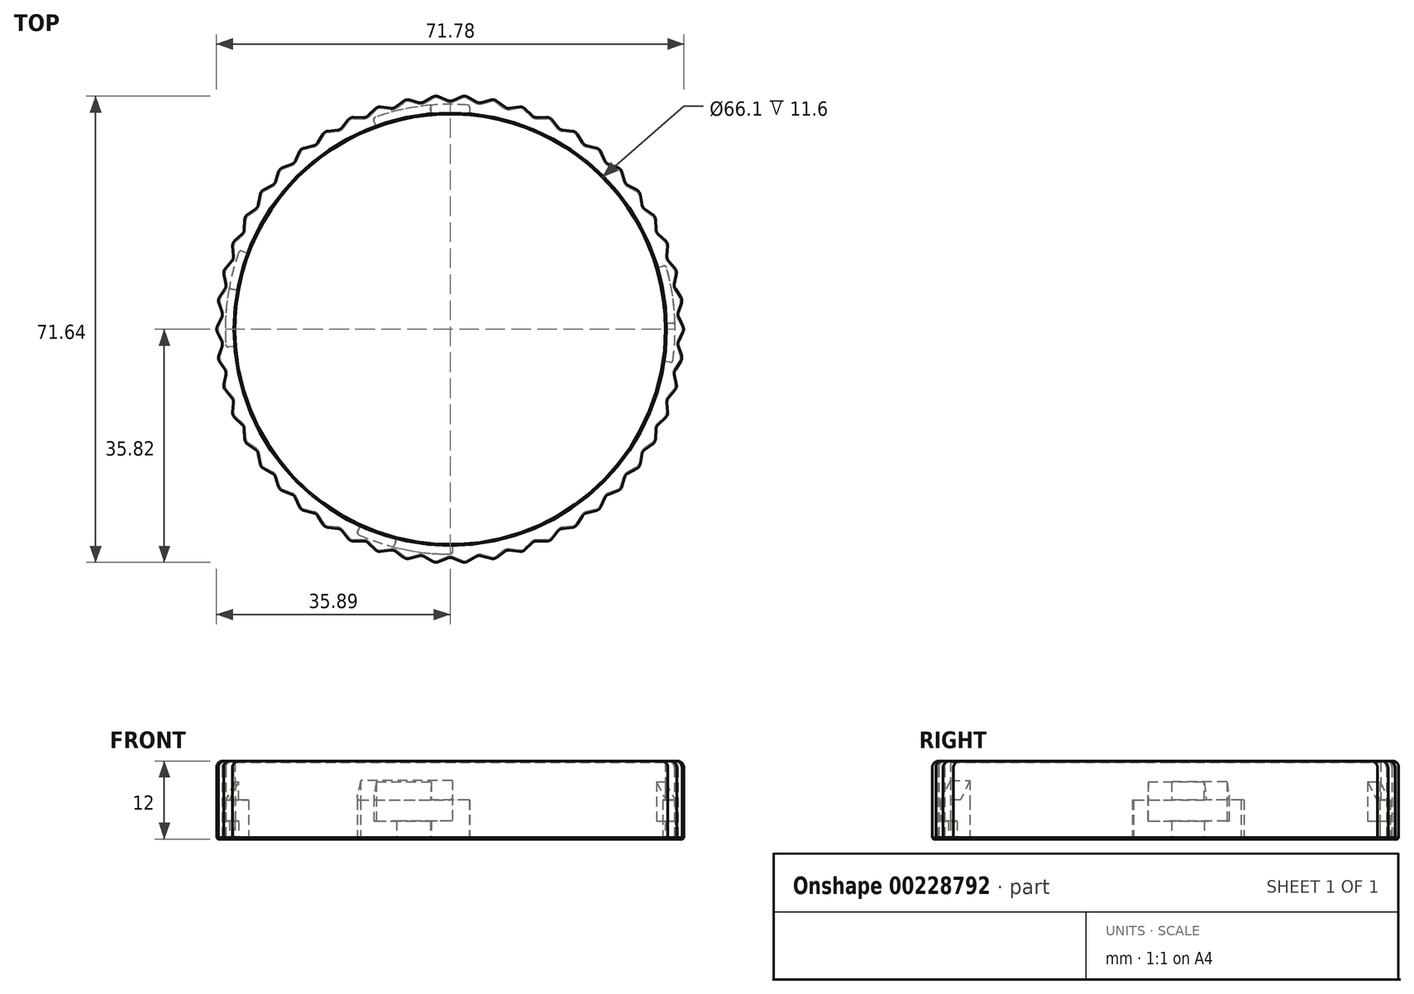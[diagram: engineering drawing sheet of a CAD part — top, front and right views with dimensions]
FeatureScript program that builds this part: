
annotation { "Feature Type Name" : "Feature", "Feature Type Description" : "" }
export const myFeature = defineFeature(function(context is Context, id is Id, definition is map)
    precondition{}
    {
        {
            var Q0;
            Q0=qCreatedBy(makeId("Top.planeOp"),FACE);
            var sketch = newSketch(context, id + "F0", { "sketchPlane" : qUnion([Q0])});
            skCircle(sketch, "E0", {"center": v(0, 0) * mm, "radius": 33.05 * mm});
            skLineSegment(sketch, "E1", {"start": v(2.68, 35.69) * mm, "end": v(4.03, 34.93) * mm});
            skLineSegment(sketch, "E2", {"start": v(4.78, 34.83) * mm, "end": v(6.28, 35.24) * mm});
            skPoint(sketch, "E3.visualSharp", {"position": v(2.26, 35.93) * mm});
            skArc(sketch, "E3.filletArc", {"start": v(2.68, 35.69) * mm, "mid": v(2.25, 35.82) * mm, "end": v(1.81, 35.74) * mm});
            skPoint(sketch, "E4.visualSharp", {"position": v(4.39, 34.72) * mm});
            skArc(sketch, "E4.filletArc", {"start": v(4.03, 34.93) * mm, "mid": v(4.4, 34.8) * mm, "end": v(4.78, 34.83) * mm});
            skPoint(sketch, "E5.visualSharp", {"position": v(6.75, 35.36) * mm});
            skArc(sketch, "E5.filletArc", {"start": v(6.72, 35.25) * mm, "mid": v(6.5, 35.27) * mm, "end": v(6.28, 35.24) * mm});
            skLineSegment(sketch, "E6.1.0", {"start": v(-1.81, 35.74) * mm, "end": v(-0.38, 35.16) * mm});
            skPoint(sketch, "E6.1.1", {"position": v(0, 35) * mm});
            skPoint(sketch, "E6.1.2", {"position": v(-2.26, 35.93) * mm});
            skArc(sketch, "E6.1.4", {"start": v(-0.38, 35.16) * mm, "mid": v(0, 35.08) * mm, "end": v(0.38, 35.16) * mm});
            skLineSegment(sketch, "E6.1.5", {"start": v(0.38, 35.16) * mm, "end": v(1.81, 35.74) * mm});
            skArc(sketch, "E6.1.6", {"start": v(-1.81, 35.74) * mm, "mid": v(-2.25, 35.82) * mm, "end": v(-2.68, 35.69) * mm});
            skArc(sketch, "E6.1.7", {"start": v(2.25, 35.82) * mm, "mid": v(2.03, 35.8) * mm, "end": v(1.81, 35.74) * mm});
            skLineSegment(sketch, "E6.2.0", {"start": v(-6.28, 35.24) * mm, "end": v(-4.78, 34.83) * mm});
            skPoint(sketch, "E6.2.1", {"position": v(-4.39, 34.72) * mm});
            skPoint(sketch, "E6.2.2", {"position": v(-6.75, 35.36) * mm});
            skPoint(sketch, "E6.2.3", {"position": v(-2.26, 35.93) * mm});
            skArc(sketch, "E6.2.4", {"start": v(-4.78, 34.83) * mm, "mid": v(-4.4, 34.8) * mm, "end": v(-4.03, 34.93) * mm});
            skLineSegment(sketch, "E6.2.5", {"start": v(-4.03, 34.93) * mm, "end": v(-2.68, 35.69) * mm});
            skArc(sketch, "E6.2.6", {"start": v(-6.28, 35.24) * mm, "mid": v(-6.72, 35.25) * mm, "end": v(-7.14, 35.07) * mm});
            skArc(sketch, "E6.2.7", {"start": v(-2.25, 35.82) * mm, "mid": v(-2.48, 35.78) * mm, "end": v(-2.68, 35.69) * mm});
            skLineSegment(sketch, "E6.3.0", {"start": v(-10.64, 34.17) * mm, "end": v(-9.11, 33.96) * mm});
            skPoint(sketch, "E6.3.1", {"position": v(-8.7, 33.9) * mm});
            skPoint(sketch, "E6.3.2", {"position": v(-11.12, 34.24) * mm});
            skPoint(sketch, "E6.3.3", {"position": v(-6.75, 35.36) * mm});
            skArc(sketch, "E6.3.4", {"start": v(-9.11, 33.96) * mm, "mid": v(-8.72, 33.98) * mm, "end": v(-8.37, 34.15) * mm});
            skLineSegment(sketch, "E6.3.5", {"start": v(-8.37, 34.15) * mm, "end": v(-7.14, 35.07) * mm});
            skArc(sketch, "E6.3.6", {"start": v(-10.64, 34.17) * mm, "mid": v(-11.09, 34.13) * mm, "end": v(-11.47, 33.9) * mm});
            skArc(sketch, "E6.3.7", {"start": v(-6.72, 35.25) * mm, "mid": v(-6.94, 35.19) * mm, "end": v(-7.14, 35.07) * mm});
            skLineSegment(sketch, "E6.4.0", {"start": v(-14.84, 32.57) * mm, "end": v(-13.3, 32.55) * mm});
            skPoint(sketch, "E6.4.1", {"position": v(-12.88, 32.54) * mm});
            skPoint(sketch, "E6.4.2", {"position": v(-15.33, 32.57) * mm});
            skPoint(sketch, "E6.4.3", {"position": v(-11.12, 34.24) * mm});
            skArc(sketch, "E6.4.4", {"start": v(-13.3, 32.55) * mm, "mid": v(-12.91, 32.62) * mm, "end": v(-12.59, 32.83) * mm});
            skLineSegment(sketch, "E6.4.5", {"start": v(-12.59, 32.83) * mm, "end": v(-11.47, 33.9) * mm});
            skArc(sketch, "E6.4.6", {"start": v(-14.84, 32.57) * mm, "mid": v(-15.28, 32.47) * mm, "end": v(-15.63, 32.2) * mm});
            skArc(sketch, "E6.4.7", {"start": v(-11.09, 34.13) * mm, "mid": v(-11.3, 34.04) * mm, "end": v(-11.47, 33.9) * mm});
            skLineSegment(sketch, "E6.5.0", {"start": v(-18.8, 30.45) * mm, "end": v(-17.27, 30.62) * mm});
            skPoint(sketch, "E6.5.1", {"position": v(-16.86, 30.67) * mm});
            skPoint(sketch, "E6.5.2", {"position": v(-19.29, 30.4) * mm});
            skPoint(sketch, "E6.5.3", {"position": v(-15.33, 32.57) * mm});
            skArc(sketch, "E6.5.4", {"start": v(-17.27, 30.62) * mm, "mid": v(-16.9, 30.74) * mm, "end": v(-16.6, 31) * mm});
            skLineSegment(sketch, "E6.5.5", {"start": v(-16.6, 31) * mm, "end": v(-15.63, 32.2) * mm});
            skArc(sketch, "E6.5.6", {"start": v(-18.8, 30.45) * mm, "mid": v(-19.23, 30.3) * mm, "end": v(-19.55, 29.98) * mm});
            skArc(sketch, "E6.5.7", {"start": v(-15.28, 32.47) * mm, "mid": v(-15.47, 32.35) * mm, "end": v(-15.63, 32.2) * mm});
            skLineSegment(sketch, "E6.6.0", {"start": v(-22.47, 27.85) * mm, "end": v(-20.97, 28.22) * mm});
            skPoint(sketch, "E6.6.1", {"position": v(-20.57, 28.32) * mm});
            skPoint(sketch, "E6.6.2", {"position": v(-22.95, 27.74) * mm});
            skPoint(sketch, "E6.6.3", {"position": v(-19.29, 30.4) * mm});
            skArc(sketch, "E6.6.4", {"start": v(-20.97, 28.22) * mm, "mid": v(-20.62, 28.38) * mm, "end": v(-20.36, 28.67) * mm});
            skLineSegment(sketch, "E6.6.5", {"start": v(-20.36, 28.67) * mm, "end": v(-19.55, 29.98) * mm});
            skArc(sketch, "E6.6.6", {"start": v(-22.47, 27.85) * mm, "mid": v(-22.88, 27.65) * mm, "end": v(-23.15, 27.3) * mm});
            skArc(sketch, "E6.6.7", {"start": v(-19.23, 30.3) * mm, "mid": v(-19.4, 30.16) * mm, "end": v(-19.55, 29.98) * mm});
            skLineSegment(sketch, "E6.7.0", {"start": v(-25.79, 24.82) * mm, "end": v(-24.34, 25.37) * mm});
            skPoint(sketch, "E6.7.1", {"position": v(-23.96, 25.51) * mm});
            skPoint(sketch, "E6.7.2", {"position": v(-26.24, 24.64) * mm});
            skPoint(sketch, "E6.7.3", {"position": v(-22.95, 27.74) * mm});
            skArc(sketch, "E6.7.4", {"start": v(-24.34, 25.37) * mm, "mid": v(-24.01, 25.57) * mm, "end": v(-23.79, 25.89) * mm});
            skLineSegment(sketch, "E6.7.5", {"start": v(-23.79, 25.89) * mm, "end": v(-23.15, 27.3) * mm});
            skArc(sketch, "E6.7.6", {"start": v(-25.79, 24.82) * mm, "mid": v(-26.16, 24.57) * mm, "end": v(-26.39, 24.18) * mm});
            skArc(sketch, "E6.7.7", {"start": v(-22.88, 27.65) * mm, "mid": v(-23.03, 27.49) * mm, "end": v(-23.15, 27.3) * mm});
            skLineSegment(sketch, "E6.8.0", {"start": v(-28.7, 21.39) * mm, "end": v(-27.33, 22.12) * mm});
            skPoint(sketch, "E6.8.1", {"position": v(-26.97, 22.3) * mm});
            skPoint(sketch, "E6.8.2", {"position": v(-29.12, 21.16) * mm});
            skPoint(sketch, "E6.8.3", {"position": v(-26.24, 24.64) * mm});
            skArc(sketch, "E6.8.4", {"start": v(-27.33, 22.12) * mm, "mid": v(-27.03, 22.36) * mm, "end": v(-26.85, 22.7) * mm});
            skLineSegment(sketch, "E6.8.5", {"start": v(-26.85, 22.7) * mm, "end": v(-26.39, 24.18) * mm});
            skArc(sketch, "E6.8.6", {"start": v(-28.7, 21.39) * mm, "mid": v(-29.03, 21.1) * mm, "end": v(-29.2, 20.68) * mm});
            skArc(sketch, "E6.8.7", {"start": v(-26.16, 24.57) * mm, "mid": v(-26.3, 24.39) * mm, "end": v(-26.39, 24.18) * mm});
            skLineSegment(sketch, "E6.9.0", {"start": v(-31.15, 17.62) * mm, "end": v(-29.89, 18.52) * mm});
            skPoint(sketch, "E6.9.1", {"position": v(-29.55, 18.75) * mm});
            skPoint(sketch, "E6.9.2", {"position": v(-31.55, 17.34) * mm});
            skPoint(sketch, "E6.9.3", {"position": v(-29.12, 21.16) * mm});
            skArc(sketch, "E6.9.4", {"start": v(-29.89, 18.52) * mm, "mid": v(-29.62, 18.8) * mm, "end": v(-29.48, 19.16) * mm});
            skLineSegment(sketch, "E6.9.5", {"start": v(-29.48, 19.16) * mm, "end": v(-29.2, 20.68) * mm});
            skArc(sketch, "E6.9.6", {"start": v(-31.15, 17.62) * mm, "mid": v(-31.45, 17.29) * mm, "end": v(-31.57, 16.86) * mm});
            skArc(sketch, "E6.9.7", {"start": v(-29.03, 21.1) * mm, "mid": v(-29.15, 20.9) * mm, "end": v(-29.2, 20.68) * mm});
            skLineSegment(sketch, "E6.10.0", {"start": v(-33.11, 13.58) * mm, "end": v(-31.97, 14.62) * mm});
            skPoint(sketch, "E6.10.1", {"position": v(-31.67, 14.9) * mm});
            skPoint(sketch, "E6.10.2", {"position": v(-33.47, 13.25) * mm});
            skPoint(sketch, "E6.10.3", {"position": v(-31.55, 17.34) * mm});
            skArc(sketch, "E6.10.4", {"start": v(-31.97, 14.62) * mm, "mid": v(-31.74, 14.94) * mm, "end": v(-31.65, 15.31) * mm});
            skLineSegment(sketch, "E6.10.5", {"start": v(-31.65, 15.31) * mm, "end": v(-31.57, 16.86) * mm});
            skArc(sketch, "E6.10.6", {"start": v(-33.11, 13.58) * mm, "mid": v(-33.37, 13.21) * mm, "end": v(-33.44, 12.77) * mm});
            skArc(sketch, "E6.10.7", {"start": v(-31.45, 17.29) * mm, "mid": v(-31.53, 17.08) * mm, "end": v(-31.57, 16.86) * mm});
            skLineSegment(sketch, "E6.11.0", {"start": v(-34.55, 9.32) * mm, "end": v(-33.55, 10.5) * mm});
            skPoint(sketch, "E6.11.1", {"position": v(-33.29, 10.82) * mm});
            skPoint(sketch, "E6.11.2", {"position": v(-34.87, 8.95) * mm});
            skPoint(sketch, "E6.11.3", {"position": v(-33.47, 13.25) * mm});
            skArc(sketch, "E6.11.4", {"start": v(-33.55, 10.5) * mm, "mid": v(-33.36, 10.84) * mm, "end": v(-33.32, 11.23) * mm});
            skLineSegment(sketch, "E6.11.5", {"start": v(-33.32, 11.23) * mm, "end": v(-33.44, 12.77) * mm});
            skArc(sketch, "E6.11.6", {"start": v(-34.55, 9.32) * mm, "mid": v(-34.76, 8.92) * mm, "end": v(-34.77, 8.48) * mm});
            skArc(sketch, "E6.11.7", {"start": v(-33.37, 13.21) * mm, "mid": v(-33.43, 13) * mm, "end": v(-33.44, 12.77) * mm});
            skLineSegment(sketch, "E6.12.0", {"start": v(-35.45, 4.92) * mm, "end": v(-34.6, 6.21) * mm});
            skPoint(sketch, "E6.12.1", {"position": v(-34.38, 6.56) * mm});
            skPoint(sketch, "E6.12.2", {"position": v(-35.72, 4.51) * mm});
            skPoint(sketch, "E6.12.3", {"position": v(-34.87, 8.95) * mm});
            skArc(sketch, "E6.12.4", {"start": v(-34.6, 6.21) * mm, "mid": v(-34.46, 6.57) * mm, "end": v(-34.46, 6.96) * mm});
            skLineSegment(sketch, "E6.12.5", {"start": v(-34.46, 6.96) * mm, "end": v(-34.77, 8.48) * mm});
            skArc(sketch, "E6.12.6", {"start": v(-35.45, 4.92) * mm, "mid": v(-35.6, 4.5) * mm, "end": v(-35.56, 4.05) * mm});
            skArc(sketch, "E6.12.7", {"start": v(-34.76, 8.92) * mm, "mid": v(-34.8, 8.7) * mm, "end": v(-34.77, 8.48) * mm});
            skLineSegment(sketch, "E6.13.0", {"start": v(-35.79, 0.44) * mm, "end": v(-35.11, 1.83) * mm});
            skPoint(sketch, "E6.13.1", {"position": v(-34.93, 2.2) * mm});
            skPoint(sketch, "E6.13.2", {"position": v(-36, 0) * mm});
            skPoint(sketch, "E6.13.3", {"position": v(-35.72, 4.51) * mm});
            skArc(sketch, "E6.13.4", {"start": v(-35.11, 1.83) * mm, "mid": v(-35.01, 2.2) * mm, "end": v(-35.06, 2.59) * mm});
            skLineSegment(sketch, "E6.13.5", {"start": v(-35.06, 2.59) * mm, "end": v(-35.56, 4.05) * mm});
            skArc(sketch, "E6.13.6", {"start": v(-35.79, 0.44) * mm, "mid": v(-35.89, 0) * mm, "end": v(-35.79, -0.44) * mm});
            skArc(sketch, "E6.13.7", {"start": v(-35.6, 4.5) * mm, "mid": v(-35.6, 4.27) * mm, "end": v(-35.56, 4.05) * mm});
            skLineSegment(sketch, "E6.14.0", {"start": v(-35.56, -4.05) * mm, "end": v(-35.06, -2.59) * mm});
            skPoint(sketch, "E6.14.1", {"position": v(-34.93, -2.2) * mm});
            skPoint(sketch, "E6.14.2", {"position": v(-35.72, -4.51) * mm});
            skPoint(sketch, "E6.14.3", {"position": v(-36, 0) * mm});
            skArc(sketch, "E6.14.4", {"start": v(-35.06, -2.59) * mm, "mid": v(-35.01, -2.2) * mm, "end": v(-35.11, -1.83) * mm});
            skLineSegment(sketch, "E6.14.5", {"start": v(-35.11, -1.83) * mm, "end": v(-35.79, -0.44) * mm});
            skArc(sketch, "E6.14.6", {"start": v(-35.56, -4.05) * mm, "mid": v(-35.6, -4.5) * mm, "end": v(-35.45, -4.92) * mm});
            skArc(sketch, "E6.14.7", {"start": v(-35.89, 0) * mm, "mid": v(-35.86, -0.22) * mm, "end": v(-35.79, -0.44) * mm});
            skLineSegment(sketch, "E6.15.0", {"start": v(-34.77, -8.48) * mm, "end": v(-34.46, -6.96) * mm});
            skPoint(sketch, "E6.15.1", {"position": v(-34.38, -6.56) * mm});
            skPoint(sketch, "E6.15.2", {"position": v(-34.87, -8.95) * mm});
            skPoint(sketch, "E6.15.3", {"position": v(-35.72, -4.51) * mm});
            skArc(sketch, "E6.15.4", {"start": v(-34.46, -6.96) * mm, "mid": v(-34.46, -6.57) * mm, "end": v(-34.6, -6.21) * mm});
            skLineSegment(sketch, "E6.15.5", {"start": v(-34.6, -6.21) * mm, "end": v(-35.45, -4.92) * mm});
            skArc(sketch, "E6.15.6", {"start": v(-34.77, -8.48) * mm, "mid": v(-34.76, -8.92) * mm, "end": v(-34.55, -9.32) * mm});
            skArc(sketch, "E6.15.7", {"start": v(-35.6, -4.5) * mm, "mid": v(-35.55, -4.72) * mm, "end": v(-35.45, -4.92) * mm});
            skLineSegment(sketch, "E6.16.0", {"start": v(-33.44, -12.77) * mm, "end": v(-33.32, -11.23) * mm});
            skPoint(sketch, "E6.16.1", {"position": v(-33.29, -10.82) * mm});
            skPoint(sketch, "E6.16.2", {"position": v(-33.47, -13.25) * mm});
            skPoint(sketch, "E6.16.3", {"position": v(-34.87, -8.95) * mm});
            skArc(sketch, "E6.16.4", {"start": v(-33.32, -11.23) * mm, "mid": v(-33.36, -10.84) * mm, "end": v(-33.55, -10.5) * mm});
            skLineSegment(sketch, "E6.16.5", {"start": v(-33.55, -10.5) * mm, "end": v(-34.55, -9.32) * mm});
            skArc(sketch, "E6.16.6", {"start": v(-33.44, -12.77) * mm, "mid": v(-33.37, -13.21) * mm, "end": v(-33.11, -13.58) * mm});
            skArc(sketch, "E6.16.7", {"start": v(-34.76, -8.92) * mm, "mid": v(-34.68, -9.14) * mm, "end": v(-34.55, -9.32) * mm});
            skLineSegment(sketch, "E6.17.0", {"start": v(-31.57, -16.86) * mm, "end": v(-31.65, -15.31) * mm});
            skPoint(sketch, "E6.17.1", {"position": v(-31.67, -14.9) * mm});
            skPoint(sketch, "E6.17.2", {"position": v(-31.55, -17.34) * mm});
            skPoint(sketch, "E6.17.3", {"position": v(-33.47, -13.25) * mm});
            skArc(sketch, "E6.17.4", {"start": v(-31.65, -15.31) * mm, "mid": v(-31.74, -14.94) * mm, "end": v(-31.97, -14.62) * mm});
            skLineSegment(sketch, "E6.17.5", {"start": v(-31.97, -14.62) * mm, "end": v(-33.11, -13.58) * mm});
            skArc(sketch, "E6.17.6", {"start": v(-31.57, -16.86) * mm, "mid": v(-31.45, -17.29) * mm, "end": v(-31.15, -17.62) * mm});
            skArc(sketch, "E6.17.7", {"start": v(-33.37, -13.21) * mm, "mid": v(-33.26, -13.41) * mm, "end": v(-33.11, -13.58) * mm});
            skLineSegment(sketch, "E6.18.0", {"start": v(-29.2, -20.68) * mm, "end": v(-29.48, -19.16) * mm});
            skPoint(sketch, "E6.18.1", {"position": v(-29.55, -18.75) * mm});
            skPoint(sketch, "E6.18.2", {"position": v(-29.12, -21.16) * mm});
            skPoint(sketch, "E6.18.3", {"position": v(-31.55, -17.34) * mm});
            skArc(sketch, "E6.18.4", {"start": v(-29.48, -19.16) * mm, "mid": v(-29.62, -18.8) * mm, "end": v(-29.89, -18.52) * mm});
            skLineSegment(sketch, "E6.18.5", {"start": v(-29.89, -18.52) * mm, "end": v(-31.15, -17.62) * mm});
            skArc(sketch, "E6.18.6", {"start": v(-29.2, -20.68) * mm, "mid": v(-29.03, -21.1) * mm, "end": v(-28.7, -21.39) * mm});
            skArc(sketch, "E6.18.7", {"start": v(-31.45, -17.29) * mm, "mid": v(-31.32, -17.47) * mm, "end": v(-31.15, -17.62) * mm});
            skLineSegment(sketch, "E6.19.0", {"start": v(-26.39, -24.18) * mm, "end": v(-26.85, -22.7) * mm});
            skPoint(sketch, "E6.19.1", {"position": v(-26.97, -22.3) * mm});
            skPoint(sketch, "E6.19.2", {"position": v(-26.24, -24.64) * mm});
            skPoint(sketch, "E6.19.3", {"position": v(-29.12, -21.16) * mm});
            skArc(sketch, "E6.19.4", {"start": v(-26.85, -22.7) * mm, "mid": v(-27.03, -22.36) * mm, "end": v(-27.33, -22.12) * mm});
            skLineSegment(sketch, "E6.19.5", {"start": v(-27.33, -22.12) * mm, "end": v(-28.7, -21.39) * mm});
            skArc(sketch, "E6.19.6", {"start": v(-26.39, -24.18) * mm, "mid": v(-26.16, -24.57) * mm, "end": v(-25.79, -24.82) * mm});
            skArc(sketch, "E6.19.7", {"start": v(-29.03, -21.1) * mm, "mid": v(-28.88, -21.26) * mm, "end": v(-28.7, -21.39) * mm});
            skLineSegment(sketch, "E6.20.0", {"start": v(-23.15, -27.3) * mm, "end": v(-23.79, -25.89) * mm});
            skPoint(sketch, "E6.20.1", {"position": v(-23.96, -25.51) * mm});
            skPoint(sketch, "E6.20.2", {"position": v(-22.95, -27.74) * mm});
            skPoint(sketch, "E6.20.3", {"position": v(-26.24, -24.64) * mm});
            skArc(sketch, "E6.20.4", {"start": v(-23.79, -25.89) * mm, "mid": v(-24.01, -25.57) * mm, "end": v(-24.34, -25.37) * mm});
            skLineSegment(sketch, "E6.20.5", {"start": v(-24.34, -25.37) * mm, "end": v(-25.79, -24.82) * mm});
            skArc(sketch, "E6.20.6", {"start": v(-23.15, -27.3) * mm, "mid": v(-22.88, -27.65) * mm, "end": v(-22.47, -27.85) * mm});
            skArc(sketch, "E6.20.7", {"start": v(-26.16, -24.57) * mm, "mid": v(-25.99, -24.71) * mm, "end": v(-25.79, -24.82) * mm});
            skLineSegment(sketch, "E6.21.0", {"start": v(-19.55, -29.98) * mm, "end": v(-20.36, -28.67) * mm});
            skPoint(sketch, "E6.21.1", {"position": v(-20.57, -28.32) * mm});
            skPoint(sketch, "E6.21.2", {"position": v(-19.29, -30.4) * mm});
            skPoint(sketch, "E6.21.3", {"position": v(-22.95, -27.74) * mm});
            skArc(sketch, "E6.21.4", {"start": v(-20.36, -28.67) * mm, "mid": v(-20.62, -28.38) * mm, "end": v(-20.97, -28.22) * mm});
            skLineSegment(sketch, "E6.21.5", {"start": v(-20.97, -28.22) * mm, "end": v(-22.47, -27.85) * mm});
            skArc(sketch, "E6.21.6", {"start": v(-19.55, -29.98) * mm, "mid": v(-19.23, -30.3) * mm, "end": v(-18.8, -30.45) * mm});
            skArc(sketch, "E6.21.7", {"start": v(-22.88, -27.65) * mm, "mid": v(-22.69, -27.78) * mm, "end": v(-22.47, -27.85) * mm});
            skLineSegment(sketch, "E6.22.0", {"start": v(-15.63, -32.2) * mm, "end": v(-16.6, -31) * mm});
            skPoint(sketch, "E6.22.1", {"position": v(-16.86, -30.67) * mm});
            skPoint(sketch, "E6.22.2", {"position": v(-15.33, -32.57) * mm});
            skPoint(sketch, "E6.22.3", {"position": v(-19.29, -30.4) * mm});
            skArc(sketch, "E6.22.4", {"start": v(-16.6, -31) * mm, "mid": v(-16.9, -30.74) * mm, "end": v(-17.27, -30.62) * mm});
            skLineSegment(sketch, "E6.22.5", {"start": v(-17.27, -30.62) * mm, "end": v(-18.8, -30.45) * mm});
            skArc(sketch, "E6.22.6", {"start": v(-15.63, -32.2) * mm, "mid": v(-15.28, -32.47) * mm, "end": v(-14.84, -32.57) * mm});
            skArc(sketch, "E6.22.7", {"start": v(-19.23, -30.3) * mm, "mid": v(-19.03, -30.4) * mm, "end": v(-18.8, -30.45) * mm});
            skLineSegment(sketch, "E6.23.0", {"start": v(-11.47, -33.9) * mm, "end": v(-12.59, -32.83) * mm});
            skPoint(sketch, "E6.23.1", {"position": v(-12.88, -32.54) * mm});
            skPoint(sketch, "E6.23.2", {"position": v(-11.12, -34.24) * mm});
            skPoint(sketch, "E6.23.3", {"position": v(-15.33, -32.57) * mm});
            skArc(sketch, "E6.23.4", {"start": v(-12.59, -32.83) * mm, "mid": v(-12.91, -32.62) * mm, "end": v(-13.3, -32.55) * mm});
            skLineSegment(sketch, "E6.23.5", {"start": v(-13.3, -32.55) * mm, "end": v(-14.84, -32.57) * mm});
            skArc(sketch, "E6.23.6", {"start": v(-11.47, -33.9) * mm, "mid": v(-11.09, -34.13) * mm, "end": v(-10.64, -34.17) * mm});
            skArc(sketch, "E6.23.7", {"start": v(-15.28, -32.47) * mm, "mid": v(-15.07, -32.54) * mm, "end": v(-14.84, -32.57) * mm});
            skLineSegment(sketch, "E6.24.0", {"start": v(-7.14, -35.07) * mm, "end": v(-8.37, -34.15) * mm});
            skPoint(sketch, "E6.24.1", {"position": v(-8.7, -33.9) * mm});
            skPoint(sketch, "E6.24.2", {"position": v(-6.75, -35.36) * mm});
            skPoint(sketch, "E6.24.3", {"position": v(-11.12, -34.24) * mm});
            skArc(sketch, "E6.24.4", {"start": v(-8.37, -34.15) * mm, "mid": v(-8.72, -33.98) * mm, "end": v(-9.11, -33.96) * mm});
            skLineSegment(sketch, "E6.24.5", {"start": v(-9.11, -33.96) * mm, "end": v(-10.64, -34.17) * mm});
            skArc(sketch, "E6.24.6", {"start": v(-7.14, -35.07) * mm, "mid": v(-6.72, -35.25) * mm, "end": v(-6.28, -35.24) * mm});
            skArc(sketch, "E6.24.7", {"start": v(-11.09, -34.13) * mm, "mid": v(-10.87, -34.18) * mm, "end": v(-10.64, -34.17) * mm});
            skLineSegment(sketch, "E6.25.0", {"start": v(-2.68, -35.69) * mm, "end": v(-4.03, -34.93) * mm});
            skPoint(sketch, "E6.25.1", {"position": v(-4.39, -34.72) * mm});
            skPoint(sketch, "E6.25.2", {"position": v(-2.26, -35.93) * mm});
            skPoint(sketch, "E6.25.3", {"position": v(-6.75, -35.36) * mm});
            skArc(sketch, "E6.25.4", {"start": v(-4.03, -34.93) * mm, "mid": v(-4.4, -34.8) * mm, "end": v(-4.78, -34.83) * mm});
            skLineSegment(sketch, "E6.25.5", {"start": v(-4.78, -34.83) * mm, "end": v(-6.28, -35.24) * mm});
            skArc(sketch, "E6.25.6", {"start": v(-2.68, -35.69) * mm, "mid": v(-2.25, -35.82) * mm, "end": v(-1.81, -35.74) * mm});
            skArc(sketch, "E6.25.7", {"start": v(-6.72, -35.25) * mm, "mid": v(-6.5, -35.27) * mm, "end": v(-6.28, -35.24) * mm});
            skLineSegment(sketch, "E6.26.0", {"start": v(1.81, -35.74) * mm, "end": v(0.38, -35.16) * mm});
            skPoint(sketch, "E6.26.1", {"position": v(0, -35) * mm});
            skPoint(sketch, "E6.26.2", {"position": v(2.26, -35.93) * mm});
            skPoint(sketch, "E6.26.3", {"position": v(-2.26, -35.93) * mm});
            skArc(sketch, "E6.26.4", {"start": v(0.38, -35.16) * mm, "mid": v(0, -35.08) * mm, "end": v(-0.38, -35.16) * mm});
            skLineSegment(sketch, "E6.26.5", {"start": v(-0.38, -35.16) * mm, "end": v(-1.81, -35.74) * mm});
            skArc(sketch, "E6.26.6", {"start": v(1.81, -35.74) * mm, "mid": v(2.25, -35.82) * mm, "end": v(2.68, -35.69) * mm});
            skArc(sketch, "E6.26.7", {"start": v(-2.25, -35.82) * mm, "mid": v(-2.03, -35.8) * mm, "end": v(-1.81, -35.74) * mm});
            skLineSegment(sketch, "E6.27.0", {"start": v(6.28, -35.24) * mm, "end": v(4.78, -34.83) * mm});
            skPoint(sketch, "E6.27.1", {"position": v(4.39, -34.72) * mm});
            skPoint(sketch, "E6.27.2", {"position": v(6.75, -35.36) * mm});
            skPoint(sketch, "E6.27.3", {"position": v(2.26, -35.93) * mm});
            skArc(sketch, "E6.27.4", {"start": v(4.78, -34.83) * mm, "mid": v(4.4, -34.8) * mm, "end": v(4.03, -34.93) * mm});
            skLineSegment(sketch, "E6.27.5", {"start": v(4.03, -34.93) * mm, "end": v(2.68, -35.69) * mm});
            skArc(sketch, "E6.27.6", {"start": v(6.28, -35.24) * mm, "mid": v(6.72, -35.25) * mm, "end": v(7.14, -35.07) * mm});
            skArc(sketch, "E6.27.7", {"start": v(2.25, -35.82) * mm, "mid": v(2.48, -35.78) * mm, "end": v(2.68, -35.69) * mm});
            skLineSegment(sketch, "E6.28.0", {"start": v(10.64, -34.17) * mm, "end": v(9.11, -33.96) * mm});
            skPoint(sketch, "E6.28.1", {"position": v(8.7, -33.9) * mm});
            skPoint(sketch, "E6.28.2", {"position": v(11.12, -34.24) * mm});
            skPoint(sketch, "E6.28.3", {"position": v(6.75, -35.36) * mm});
            skArc(sketch, "E6.28.4", {"start": v(9.11, -33.96) * mm, "mid": v(8.72, -33.98) * mm, "end": v(8.37, -34.15) * mm});
            skLineSegment(sketch, "E6.28.5", {"start": v(8.37, -34.15) * mm, "end": v(7.14, -35.07) * mm});
            skArc(sketch, "E6.28.6", {"start": v(10.64, -34.17) * mm, "mid": v(11.09, -34.13) * mm, "end": v(11.47, -33.9) * mm});
            skArc(sketch, "E6.28.7", {"start": v(6.72, -35.25) * mm, "mid": v(6.94, -35.19) * mm, "end": v(7.14, -35.07) * mm});
            skLineSegment(sketch, "E6.29.0", {"start": v(14.84, -32.57) * mm, "end": v(13.3, -32.55) * mm});
            skPoint(sketch, "E6.29.1", {"position": v(12.88, -32.54) * mm});
            skPoint(sketch, "E6.29.2", {"position": v(15.33, -32.57) * mm});
            skPoint(sketch, "E6.29.3", {"position": v(11.12, -34.24) * mm});
            skArc(sketch, "E6.29.4", {"start": v(13.3, -32.55) * mm, "mid": v(12.91, -32.62) * mm, "end": v(12.59, -32.83) * mm});
            skLineSegment(sketch, "E6.29.5", {"start": v(12.59, -32.83) * mm, "end": v(11.47, -33.9) * mm});
            skArc(sketch, "E6.29.6", {"start": v(14.84, -32.57) * mm, "mid": v(15.28, -32.47) * mm, "end": v(15.63, -32.2) * mm});
            skArc(sketch, "E6.29.7", {"start": v(11.09, -34.13) * mm, "mid": v(11.3, -34.04) * mm, "end": v(11.47, -33.9) * mm});
            skLineSegment(sketch, "E6.30.0", {"start": v(18.8, -30.45) * mm, "end": v(17.27, -30.62) * mm});
            skPoint(sketch, "E6.30.1", {"position": v(16.86, -30.67) * mm});
            skPoint(sketch, "E6.30.2", {"position": v(19.29, -30.4) * mm});
            skPoint(sketch, "E6.30.3", {"position": v(15.33, -32.57) * mm});
            skArc(sketch, "E6.30.4", {"start": v(17.27, -30.62) * mm, "mid": v(16.9, -30.74) * mm, "end": v(16.6, -31) * mm});
            skLineSegment(sketch, "E6.30.5", {"start": v(16.6, -31) * mm, "end": v(15.63, -32.2) * mm});
            skArc(sketch, "E6.30.6", {"start": v(18.8, -30.45) * mm, "mid": v(19.23, -30.3) * mm, "end": v(19.55, -29.98) * mm});
            skArc(sketch, "E6.30.7", {"start": v(15.28, -32.47) * mm, "mid": v(15.47, -32.35) * mm, "end": v(15.63, -32.2) * mm});
            skLineSegment(sketch, "E6.31.0", {"start": v(22.47, -27.85) * mm, "end": v(20.97, -28.22) * mm});
            skPoint(sketch, "E6.31.1", {"position": v(20.57, -28.32) * mm});
            skPoint(sketch, "E6.31.2", {"position": v(22.95, -27.74) * mm});
            skPoint(sketch, "E6.31.3", {"position": v(19.29, -30.4) * mm});
            skArc(sketch, "E6.31.4", {"start": v(20.97, -28.22) * mm, "mid": v(20.62, -28.38) * mm, "end": v(20.36, -28.67) * mm});
            skLineSegment(sketch, "E6.31.5", {"start": v(20.36, -28.67) * mm, "end": v(19.55, -29.98) * mm});
            skArc(sketch, "E6.31.6", {"start": v(22.47, -27.85) * mm, "mid": v(22.88, -27.65) * mm, "end": v(23.15, -27.3) * mm});
            skArc(sketch, "E6.31.7", {"start": v(19.23, -30.3) * mm, "mid": v(19.4, -30.16) * mm, "end": v(19.55, -29.98) * mm});
            skLineSegment(sketch, "E6.32.0", {"start": v(25.79, -24.82) * mm, "end": v(24.34, -25.37) * mm});
            skPoint(sketch, "E6.32.1", {"position": v(23.96, -25.51) * mm});
            skPoint(sketch, "E6.32.2", {"position": v(26.24, -24.64) * mm});
            skPoint(sketch, "E6.32.3", {"position": v(22.95, -27.74) * mm});
            skArc(sketch, "E6.32.4", {"start": v(24.34, -25.37) * mm, "mid": v(24.01, -25.57) * mm, "end": v(23.79, -25.89) * mm});
            skLineSegment(sketch, "E6.32.5", {"start": v(23.79, -25.89) * mm, "end": v(23.15, -27.3) * mm});
            skArc(sketch, "E6.32.6", {"start": v(25.79, -24.82) * mm, "mid": v(26.16, -24.57) * mm, "end": v(26.39, -24.18) * mm});
            skArc(sketch, "E6.32.7", {"start": v(22.88, -27.65) * mm, "mid": v(23.03, -27.49) * mm, "end": v(23.15, -27.3) * mm});
            skLineSegment(sketch, "E6.33.0", {"start": v(28.7, -21.39) * mm, "end": v(27.33, -22.12) * mm});
            skPoint(sketch, "E6.33.1", {"position": v(26.97, -22.3) * mm});
            skPoint(sketch, "E6.33.2", {"position": v(29.12, -21.16) * mm});
            skPoint(sketch, "E6.33.3", {"position": v(26.24, -24.64) * mm});
            skArc(sketch, "E6.33.4", {"start": v(27.33, -22.12) * mm, "mid": v(27.03, -22.36) * mm, "end": v(26.85, -22.7) * mm});
            skLineSegment(sketch, "E6.33.5", {"start": v(26.85, -22.7) * mm, "end": v(26.39, -24.18) * mm});
            skArc(sketch, "E6.33.6", {"start": v(28.7, -21.39) * mm, "mid": v(29.03, -21.1) * mm, "end": v(29.2, -20.68) * mm});
            skArc(sketch, "E6.33.7", {"start": v(26.16, -24.57) * mm, "mid": v(26.3, -24.39) * mm, "end": v(26.39, -24.18) * mm});
            skLineSegment(sketch, "E6.34.0", {"start": v(31.15, -17.62) * mm, "end": v(29.89, -18.52) * mm});
            skPoint(sketch, "E6.34.1", {"position": v(29.55, -18.75) * mm});
            skPoint(sketch, "E6.34.2", {"position": v(31.55, -17.34) * mm});
            skPoint(sketch, "E6.34.3", {"position": v(29.12, -21.16) * mm});
            skArc(sketch, "E6.34.4", {"start": v(29.89, -18.52) * mm, "mid": v(29.62, -18.8) * mm, "end": v(29.48, -19.16) * mm});
            skLineSegment(sketch, "E6.34.5", {"start": v(29.48, -19.16) * mm, "end": v(29.2, -20.68) * mm});
            skArc(sketch, "E6.34.6", {"start": v(31.15, -17.62) * mm, "mid": v(31.45, -17.29) * mm, "end": v(31.57, -16.86) * mm});
            skArc(sketch, "E6.34.7", {"start": v(29.03, -21.1) * mm, "mid": v(29.15, -20.9) * mm, "end": v(29.2, -20.68) * mm});
            skLineSegment(sketch, "E6.35.0", {"start": v(33.11, -13.58) * mm, "end": v(31.97, -14.62) * mm});
            skPoint(sketch, "E6.35.1", {"position": v(31.67, -14.9) * mm});
            skPoint(sketch, "E6.35.2", {"position": v(33.47, -13.25) * mm});
            skPoint(sketch, "E6.35.3", {"position": v(31.55, -17.34) * mm});
            skArc(sketch, "E6.35.4", {"start": v(31.97, -14.62) * mm, "mid": v(31.74, -14.94) * mm, "end": v(31.65, -15.31) * mm});
            skLineSegment(sketch, "E6.35.5", {"start": v(31.65, -15.31) * mm, "end": v(31.57, -16.86) * mm});
            skArc(sketch, "E6.35.6", {"start": v(33.11, -13.58) * mm, "mid": v(33.37, -13.21) * mm, "end": v(33.44, -12.77) * mm});
            skArc(sketch, "E6.35.7", {"start": v(31.45, -17.29) * mm, "mid": v(31.53, -17.08) * mm, "end": v(31.57, -16.86) * mm});
            skLineSegment(sketch, "E6.36.0", {"start": v(34.55, -9.32) * mm, "end": v(33.55, -10.5) * mm});
            skPoint(sketch, "E6.36.1", {"position": v(33.29, -10.82) * mm});
            skPoint(sketch, "E6.36.2", {"position": v(34.87, -8.95) * mm});
            skPoint(sketch, "E6.36.3", {"position": v(33.47, -13.25) * mm});
            skArc(sketch, "E6.36.4", {"start": v(33.55, -10.5) * mm, "mid": v(33.36, -10.84) * mm, "end": v(33.32, -11.23) * mm});
            skLineSegment(sketch, "E6.36.5", {"start": v(33.32, -11.23) * mm, "end": v(33.44, -12.77) * mm});
            skArc(sketch, "E6.36.6", {"start": v(34.55, -9.32) * mm, "mid": v(34.76, -8.92) * mm, "end": v(34.77, -8.48) * mm});
            skArc(sketch, "E6.36.7", {"start": v(33.37, -13.21) * mm, "mid": v(33.43, -13) * mm, "end": v(33.44, -12.77) * mm});
            skLineSegment(sketch, "E6.37.0", {"start": v(35.45, -4.92) * mm, "end": v(34.6, -6.21) * mm});
            skPoint(sketch, "E6.37.1", {"position": v(34.38, -6.56) * mm});
            skPoint(sketch, "E6.37.2", {"position": v(35.72, -4.51) * mm});
            skPoint(sketch, "E6.37.3", {"position": v(34.87, -8.95) * mm});
            skArc(sketch, "E6.37.4", {"start": v(34.6, -6.21) * mm, "mid": v(34.46, -6.57) * mm, "end": v(34.46, -6.96) * mm});
            skLineSegment(sketch, "E6.37.5", {"start": v(34.46, -6.96) * mm, "end": v(34.77, -8.48) * mm});
            skArc(sketch, "E6.37.6", {"start": v(35.45, -4.92) * mm, "mid": v(35.6, -4.5) * mm, "end": v(35.56, -4.05) * mm});
            skArc(sketch, "E6.37.7", {"start": v(34.76, -8.92) * mm, "mid": v(34.8, -8.7) * mm, "end": v(34.77, -8.48) * mm});
            skLineSegment(sketch, "E6.38.0", {"start": v(35.79, -0.44) * mm, "end": v(35.11, -1.83) * mm});
            skPoint(sketch, "E6.38.1", {"position": v(34.93, -2.2) * mm});
            skPoint(sketch, "E6.38.2", {"position": v(36, 0) * mm});
            skPoint(sketch, "E6.38.3", {"position": v(35.72, -4.51) * mm});
            skArc(sketch, "E6.38.4", {"start": v(35.11, -1.83) * mm, "mid": v(35.01, -2.2) * mm, "end": v(35.06, -2.59) * mm});
            skLineSegment(sketch, "E6.38.5", {"start": v(35.06, -2.59) * mm, "end": v(35.56, -4.05) * mm});
            skArc(sketch, "E6.38.6", {"start": v(35.79, -0.44) * mm, "mid": v(35.89, 0) * mm, "end": v(35.79, 0.44) * mm});
            skArc(sketch, "E6.38.7", {"start": v(35.6, -4.5) * mm, "mid": v(35.6, -4.27) * mm, "end": v(35.56, -4.05) * mm});
            skLineSegment(sketch, "E6.39.0", {"start": v(35.56, 4.05) * mm, "end": v(35.06, 2.59) * mm});
            skPoint(sketch, "E6.39.1", {"position": v(34.93, 2.2) * mm});
            skPoint(sketch, "E6.39.2", {"position": v(35.72, 4.51) * mm});
            skPoint(sketch, "E6.39.3", {"position": v(36, 0) * mm});
            skArc(sketch, "E6.39.4", {"start": v(35.06, 2.59) * mm, "mid": v(35.01, 2.2) * mm, "end": v(35.11, 1.83) * mm});
            skLineSegment(sketch, "E6.39.5", {"start": v(35.11, 1.83) * mm, "end": v(35.79, 0.44) * mm});
            skArc(sketch, "E6.39.6", {"start": v(35.56, 4.05) * mm, "mid": v(35.6, 4.5) * mm, "end": v(35.45, 4.92) * mm});
            skArc(sketch, "E6.39.7", {"start": v(35.89, 0) * mm, "mid": v(35.86, 0.22) * mm, "end": v(35.79, 0.44) * mm});
            skLineSegment(sketch, "E6.40.0", {"start": v(34.77, 8.48) * mm, "end": v(34.46, 6.96) * mm});
            skPoint(sketch, "E6.40.1", {"position": v(34.38, 6.56) * mm});
            skPoint(sketch, "E6.40.2", {"position": v(34.87, 8.95) * mm});
            skPoint(sketch, "E6.40.3", {"position": v(35.72, 4.51) * mm});
            skArc(sketch, "E6.40.4", {"start": v(34.46, 6.96) * mm, "mid": v(34.46, 6.57) * mm, "end": v(34.6, 6.21) * mm});
            skLineSegment(sketch, "E6.40.5", {"start": v(34.6, 6.21) * mm, "end": v(35.45, 4.92) * mm});
            skArc(sketch, "E6.40.6", {"start": v(34.77, 8.48) * mm, "mid": v(34.76, 8.92) * mm, "end": v(34.55, 9.32) * mm});
            skArc(sketch, "E6.40.7", {"start": v(35.6, 4.5) * mm, "mid": v(35.55, 4.72) * mm, "end": v(35.45, 4.92) * mm});
            skLineSegment(sketch, "E6.41.0", {"start": v(33.44, 12.77) * mm, "end": v(33.32, 11.23) * mm});
            skPoint(sketch, "E6.41.1", {"position": v(33.29, 10.82) * mm});
            skPoint(sketch, "E6.41.2", {"position": v(33.47, 13.25) * mm});
            skPoint(sketch, "E6.41.3", {"position": v(34.87, 8.95) * mm});
            skArc(sketch, "E6.41.4", {"start": v(33.32, 11.23) * mm, "mid": v(33.36, 10.84) * mm, "end": v(33.55, 10.5) * mm});
            skLineSegment(sketch, "E6.41.5", {"start": v(33.55, 10.5) * mm, "end": v(34.55, 9.32) * mm});
            skArc(sketch, "E6.41.6", {"start": v(33.44, 12.77) * mm, "mid": v(33.37, 13.21) * mm, "end": v(33.11, 13.58) * mm});
            skArc(sketch, "E6.41.7", {"start": v(34.76, 8.92) * mm, "mid": v(34.68, 9.14) * mm, "end": v(34.55, 9.32) * mm});
            skLineSegment(sketch, "E6.42.0", {"start": v(31.57, 16.86) * mm, "end": v(31.65, 15.31) * mm});
            skPoint(sketch, "E6.42.1", {"position": v(31.67, 14.9) * mm});
            skPoint(sketch, "E6.42.2", {"position": v(31.55, 17.34) * mm});
            skPoint(sketch, "E6.42.3", {"position": v(33.47, 13.25) * mm});
            skArc(sketch, "E6.42.4", {"start": v(31.65, 15.31) * mm, "mid": v(31.74, 14.94) * mm, "end": v(31.97, 14.62) * mm});
            skLineSegment(sketch, "E6.42.5", {"start": v(31.97, 14.62) * mm, "end": v(33.11, 13.58) * mm});
            skArc(sketch, "E6.42.6", {"start": v(31.57, 16.86) * mm, "mid": v(31.45, 17.29) * mm, "end": v(31.15, 17.62) * mm});
            skArc(sketch, "E6.42.7", {"start": v(33.37, 13.21) * mm, "mid": v(33.26, 13.41) * mm, "end": v(33.11, 13.58) * mm});
            skLineSegment(sketch, "E6.43.0", {"start": v(29.2, 20.68) * mm, "end": v(29.48, 19.16) * mm});
            skPoint(sketch, "E6.43.1", {"position": v(29.55, 18.75) * mm});
            skPoint(sketch, "E6.43.2", {"position": v(29.12, 21.16) * mm});
            skPoint(sketch, "E6.43.3", {"position": v(31.55, 17.34) * mm});
            skArc(sketch, "E6.43.4", {"start": v(29.48, 19.16) * mm, "mid": v(29.62, 18.8) * mm, "end": v(29.89, 18.52) * mm});
            skLineSegment(sketch, "E6.43.5", {"start": v(29.89, 18.52) * mm, "end": v(31.15, 17.62) * mm});
            skArc(sketch, "E6.43.6", {"start": v(29.2, 20.68) * mm, "mid": v(29.03, 21.1) * mm, "end": v(28.7, 21.39) * mm});
            skArc(sketch, "E6.43.7", {"start": v(31.45, 17.29) * mm, "mid": v(31.32, 17.47) * mm, "end": v(31.15, 17.62) * mm});
            skLineSegment(sketch, "E6.44.0", {"start": v(26.39, 24.18) * mm, "end": v(26.85, 22.7) * mm});
            skPoint(sketch, "E6.44.1", {"position": v(26.97, 22.3) * mm});
            skPoint(sketch, "E6.44.2", {"position": v(26.24, 24.64) * mm});
            skPoint(sketch, "E6.44.3", {"position": v(29.12, 21.16) * mm});
            skArc(sketch, "E6.44.4", {"start": v(26.85, 22.7) * mm, "mid": v(27.03, 22.36) * mm, "end": v(27.33, 22.12) * mm});
            skLineSegment(sketch, "E6.44.5", {"start": v(27.33, 22.12) * mm, "end": v(28.7, 21.39) * mm});
            skArc(sketch, "E6.44.6", {"start": v(26.39, 24.18) * mm, "mid": v(26.16, 24.57) * mm, "end": v(25.79, 24.82) * mm});
            skArc(sketch, "E6.44.7", {"start": v(29.03, 21.1) * mm, "mid": v(28.88, 21.26) * mm, "end": v(28.7, 21.39) * mm});
            skLineSegment(sketch, "E6.45.0", {"start": v(23.15, 27.3) * mm, "end": v(23.79, 25.89) * mm});
            skPoint(sketch, "E6.45.1", {"position": v(23.96, 25.51) * mm});
            skPoint(sketch, "E6.45.2", {"position": v(22.95, 27.74) * mm});
            skPoint(sketch, "E6.45.3", {"position": v(26.24, 24.64) * mm});
            skArc(sketch, "E6.45.4", {"start": v(23.79, 25.89) * mm, "mid": v(24.01, 25.57) * mm, "end": v(24.34, 25.37) * mm});
            skLineSegment(sketch, "E6.45.5", {"start": v(24.34, 25.37) * mm, "end": v(25.79, 24.82) * mm});
            skArc(sketch, "E6.45.6", {"start": v(23.15, 27.3) * mm, "mid": v(22.88, 27.65) * mm, "end": v(22.47, 27.85) * mm});
            skArc(sketch, "E6.45.7", {"start": v(26.16, 24.57) * mm, "mid": v(25.99, 24.71) * mm, "end": v(25.79, 24.82) * mm});
            skLineSegment(sketch, "E6.46.0", {"start": v(19.55, 29.98) * mm, "end": v(20.36, 28.67) * mm});
            skPoint(sketch, "E6.46.1", {"position": v(20.57, 28.32) * mm});
            skPoint(sketch, "E6.46.2", {"position": v(19.29, 30.4) * mm});
            skPoint(sketch, "E6.46.3", {"position": v(22.95, 27.74) * mm});
            skArc(sketch, "E6.46.4", {"start": v(20.36, 28.67) * mm, "mid": v(20.62, 28.38) * mm, "end": v(20.97, 28.22) * mm});
            skLineSegment(sketch, "E6.46.5", {"start": v(20.97, 28.22) * mm, "end": v(22.47, 27.85) * mm});
            skArc(sketch, "E6.46.6", {"start": v(19.55, 29.98) * mm, "mid": v(19.23, 30.3) * mm, "end": v(18.8, 30.45) * mm});
            skArc(sketch, "E6.46.7", {"start": v(22.88, 27.65) * mm, "mid": v(22.69, 27.78) * mm, "end": v(22.47, 27.85) * mm});
            skLineSegment(sketch, "E6.47.0", {"start": v(15.63, 32.2) * mm, "end": v(16.6, 31) * mm});
            skPoint(sketch, "E6.47.1", {"position": v(16.86, 30.67) * mm});
            skPoint(sketch, "E6.47.2", {"position": v(15.33, 32.57) * mm});
            skPoint(sketch, "E6.47.3", {"position": v(19.29, 30.4) * mm});
            skArc(sketch, "E6.47.4", {"start": v(16.6, 31) * mm, "mid": v(16.9, 30.74) * mm, "end": v(17.27, 30.62) * mm});
            skLineSegment(sketch, "E6.47.5", {"start": v(17.27, 30.62) * mm, "end": v(18.8, 30.45) * mm});
            skArc(sketch, "E6.47.6", {"start": v(15.63, 32.2) * mm, "mid": v(15.28, 32.47) * mm, "end": v(14.84, 32.57) * mm});
            skArc(sketch, "E6.47.7", {"start": v(19.23, 30.3) * mm, "mid": v(19.03, 30.4) * mm, "end": v(18.8, 30.45) * mm});
            skLineSegment(sketch, "E6.48.0", {"start": v(11.47, 33.9) * mm, "end": v(12.59, 32.83) * mm});
            skPoint(sketch, "E6.48.1", {"position": v(12.88, 32.54) * mm});
            skPoint(sketch, "E6.48.2", {"position": v(11.12, 34.24) * mm});
            skPoint(sketch, "E6.48.3", {"position": v(15.33, 32.57) * mm});
            skArc(sketch, "E6.48.4", {"start": v(12.59, 32.83) * mm, "mid": v(12.91, 32.62) * mm, "end": v(13.3, 32.55) * mm});
            skLineSegment(sketch, "E6.48.5", {"start": v(13.3, 32.55) * mm, "end": v(14.84, 32.57) * mm});
            skArc(sketch, "E6.48.6", {"start": v(11.47, 33.9) * mm, "mid": v(11.09, 34.13) * mm, "end": v(10.64, 34.17) * mm});
            skArc(sketch, "E6.48.7", {"start": v(15.28, 32.47) * mm, "mid": v(15.07, 32.54) * mm, "end": v(14.84, 32.57) * mm});
            skLineSegment(sketch, "E6.49.0", {"start": v(7.14, 35.07) * mm, "end": v(8.37, 34.15) * mm});
            skPoint(sketch, "E6.49.1", {"position": v(8.7, 33.9) * mm});
            skPoint(sketch, "E6.49.3", {"position": v(11.12, 34.24) * mm});
            skArc(sketch, "E6.49.4", {"start": v(8.37, 34.15) * mm, "mid": v(8.72, 33.98) * mm, "end": v(9.11, 33.96) * mm});
            skLineSegment(sketch, "E6.49.5", {"start": v(9.11, 33.96) * mm, "end": v(10.64, 34.17) * mm});
            skArc(sketch, "E6.49.6", {"start": v(7.14, 35.07) * mm, "mid": v(6.72, 35.25) * mm, "end": v(6.28, 35.24) * mm});
            skArc(sketch, "E6.49.7", {"start": v(11.09, 34.13) * mm, "mid": v(10.87, 34.18) * mm, "end": v(10.64, 34.17) * mm});
            skPoint(sketch, "E7.endSnap0", {"position": v(0, 35.08) * mm});
            skLineSegment(sketch, "E8", {"start": v(-3.05, 34.41) * mm, "end": v(-2.92, 32.92) * mm});
            skLineSegment(sketch, "E9", {"start": v(3.05, 34.41) * mm, "end": v(2.92, 32.92) * mm});
            skArc(sketch, "E10.0", {"start": v(3.05, 34.41) * mm, "mid": v(0, 34.55) * mm, "end": v(-3.05, 34.41) * mm});
            skPoint(sketch, "E11.orphan", {"position": v(0, 34.55) * mm});
            skPoint(sketch, "E7.start.orphan", {"position": v(0, 33.05) * mm});
            skLineSegment(sketch, "E12.1.0", {"start": v(34.54, 0.95) * mm, "end": v(33.04, 0.9) * mm});
            skArc(sketch, "E12.1.1", {"start": v(34.16, -5.15) * mm, "mid": v(34.49, -2.1) * mm, "end": v(34.54, 0.95) * mm});
            skLineSegment(sketch, "E12.1.2", {"start": v(34.16, -5.15) * mm, "end": v(32.68, -4.93) * mm});
            skLineSegment(sketch, "E12.anchor1", {"start": v(0, 0) * mm, "end": v(-2.92, 32.92) * mm, "construction": true});
            skLineSegment(sketch, "E12.anchor2", {"start": v(0, 0) * mm, "end": v(33.04, 0.9) * mm, "construction": true});
            skLineSegment(sketch, "E13.1.0", {"start": v(-32.35, 12.14) * mm, "end": v(-30.94, 11.61) * mm});
            skArc(sketch, "E13.1.1", {"start": v(-32.35, 12.14) * mm, "mid": v(-33.3, 9.23) * mm, "end": v(-33.98, 6.25) * mm});
            skLineSegment(sketch, "E13.1.2", {"start": v(-33.98, 6.25) * mm, "end": v(-32.5, 5.98) * mm});
            skLineSegment(sketch, "E13.anchor2", {"start": v(0, 0) * mm, "end": v(-32.5, 5.98) * mm, "construction": true});
            skLineSegment(sketch, "E14.1.0", {"start": v(-14.37, -31.42) * mm, "end": v(-13.74, -30.06) * mm});
            skArc(sketch, "E14.1.1", {"start": v(-14.37, -31.42) * mm, "mid": v(-11.53, -32.57) * mm, "end": v(-8.6, -33.46) * mm});
            skLineSegment(sketch, "E14.1.2", {"start": v(-8.6, -33.46) * mm, "end": v(-8.23, -32) * mm});
            skLineSegment(sketch, "E14.anchor1", {"start": v(0, 0) * mm, "end": v(-32.35, 12.14) * mm, "construction": true});
            skLineSegment(sketch, "E14.anchor2", {"start": v(0, 0) * mm, "end": v(-14.37, -31.42) * mm, "construction": true});
            skSolve(sketch);
        }
        {
            var Q0;
            Q0=makeQuery(id+"F0.imprint","IMPRINT",FACE,{"disambiguationData":[TD([[makeQuery(id+"F0.imprint","IMPRINT",EDGE,{"derivedFrom":sQuery(id+"F0.wireOp",EDGE,"E1")}),-1.0]])]});
            var Q1;
            {var subQ0=sQuery(id+"F0.wireOp",EDGE,"E8");Q1=makeQuery(id+"F0.imprint","IMPRINT",FACE,{"disambiguationData":[TD([[makeQuery(id+"F0.imprint","IMPRINT",EDGE,{"derivedFrom":subQ0}),1.0]])]});}
            var Q2;
            {var subQ0=sQuery(id+"F0.wireOp",EDGE,"E12.1.0");Q2=makeQuery(id+"F0.imprint","IMPRINT",FACE,{"disambiguationData":[TD([[makeQuery(id+"F0.imprint","IMPRINT",EDGE,{"derivedFrom":subQ0}),1.0]])]});}
            var Q3;
            {var subQ0=sQuery(id+"F0.wireOp",EDGE,"E14.1.0");Q3=makeQuery(id+"F0.imprint","IMPRINT",FACE,{"disambiguationData":[TD([[makeQuery(id+"F0.imprint","IMPRINT",EDGE,{"derivedFrom":subQ0}),-1.0]])]});}
            var Q4;
            {var subQ0=sQuery(id+"F0.wireOp",EDGE,"E13.1.0");Q4=makeQuery(id+"F0.imprint","IMPRINT",FACE,{"disambiguationData":[TD([[makeQuery(id+"F0.imprint","IMPRINT",EDGE,{"derivedFrom":subQ0}),-1.0]])]});}
            extrude(context, id + "F1", {"entities" : qUnion([Q0, Q1, Q2, Q3, Q4]), "depth" : 12 * mm});
        }
        {
            var Q0;
            {var subQ0=sQuery(id+"F0.wireOp",EDGE,"E14.1.0");Q0=makeQuery(id+"F0.imprint","IMPRINT",FACE,{"disambiguationData":[TD([[makeQuery(id+"F0.imprint","IMPRINT",EDGE,{"derivedFrom":subQ0}),-1.0]])]});}
            var Q1;
            {var subQ0=sQuery(id+"F0.wireOp",EDGE,"E13.1.0");Q1=makeQuery(id+"F0.imprint","IMPRINT",FACE,{"disambiguationData":[TD([[makeQuery(id+"F0.imprint","IMPRINT",EDGE,{"derivedFrom":subQ0}),-1.0]])]});}
            var Q2;
            {var subQ0=sQuery(id+"F0.wireOp",EDGE,"E12.1.0");Q2=makeQuery(id+"F0.imprint","IMPRINT",FACE,{"disambiguationData":[TD([[makeQuery(id+"F0.imprint","IMPRINT",EDGE,{"derivedFrom":subQ0}),1.0]])]});}
            var Q3;
            {var subQ0=sQuery(id+"F0.wireOp",EDGE,"E8");Q3=makeQuery(id+"F0.imprint","IMPRINT",FACE,{"disambiguationData":[TD([[makeQuery(id+"F0.imprint","IMPRINT",EDGE,{"derivedFrom":subQ0}),1.0]])]});}
            extrude(context, id + "F2", {"entities" : qUnion([Q0, Q1, Q2, Q3]), "operationType" : NewBodyOperationType.REMOVE, "depth" : 6 * mm});
        }
        {
            var Q0;
            Q0=makeQuery(id+"F2.boolean.opBoolean","COPY",FACE,{"derivedFrom":makeQuery(id+"F2.opExtrude","SWEPT_FACE",FACE,{"disambiguationData":[OSD([sQuery(id+"F0.wireOp",EDGE,"E14.1.2")])]})});
            var sketch = newSketch(context, id + "F3", { "sketchPlane" : qUnion([Q0])});
            skLineSegment(sketch, "E15", {"start": v(33.05, 0) * mm, "end": v(33.05, 2.8) * mm});
            skLineSegment(sketch, "E16", {"start": v(33.05, 2.8) * mm, "end": v(34.55, 2.8) * mm});
            skLineSegment(sketch, "E17", {"start": v(34.55, 2.8) * mm, "end": v(34.55, 0) * mm});
            skLineSegment(sketch, "E18", {"start": v(34.55, 0) * mm, "end": v(33.05, 0) * mm});
            skLineSegment(sketch, "E19", {"start": v(33.05, 6) * mm, "end": v(33.05, 9) * mm});
            skLineSegment(sketch, "E20", {"start": v(33.05, 9) * mm, "end": v(34.55, 6) * mm});
            skLineSegment(sketch, "E21", {"start": v(34.55, 6) * mm, "end": v(33.05, 6) * mm});
            skLineSegment(sketch, "E22", {"start": v(0, 0) * mm, "end": v(0, -42.44) * mm});
            skSolve(sketch);
        }
        {
            var Q0;
            Q0=makeQuery(id+"F2.boolean.opBoolean","COPY",FACE,{"derivedFrom":makeQuery(id+"F2.opExtrude","SWEPT_FACE",FACE,{"disambiguationData":[OSD([sQuery(id+"F0.wireOp",EDGE,"E12.1.0")])]})});
            var sketch = newSketch(context, id + "F4", { "sketchPlane" : qUnion([Q0])});
            skLineSegment(sketch, "E23", {"start": v(33.05, 0) * mm, "end": v(33.05, 2.8) * mm});
            skLineSegment(sketch, "E24", {"start": v(33.05, 2.8) * mm, "end": v(34.55, 2.8) * mm});
            skLineSegment(sketch, "E25", {"start": v(33.05, 2.8) * mm, "end": v(33.05, 8.8) * mm});
            skLineSegment(sketch, "E26", {"start": v(33.05, 8.8) * mm, "end": v(34.55, 6) * mm});
            skLineSegment(sketch, "E27", {"start": v(34.55, 6) * mm, "end": v(33.05, 6) * mm});
            skSolve(sketch);
        }
        {
            var Q0;
            Q0=makeQuery(id+"F2.boolean.opBoolean","COPY",FACE,{"derivedFrom":makeQuery(id+"F2.opExtrude","SWEPT_FACE",FACE,{"disambiguationData":[OSD([sQuery(id+"F0.wireOp",EDGE,"E8")])]})});
            var sketch = newSketch(context, id + "F5", { "sketchPlane" : qUnion([Q0])});
            skLineSegment(sketch, "E28", {"start": v(33.05, 0) * mm, "end": v(33.05, 2.8) * mm});
            skLineSegment(sketch, "E29", {"start": v(33.05, 2.8) * mm, "end": v(34.55, 2.8) * mm});
            skLineSegment(sketch, "E30", {"start": v(33.05, 2.8) * mm, "end": v(33.05, 8.8) * mm});
            skLineSegment(sketch, "E31", {"start": v(33.05, 8.8) * mm, "end": v(34.55, 6) * mm});
            skSolve(sketch);
        }
        {
            var Q0;
            Q0=makeQuery(id+"F2.boolean.opBoolean","COPY",FACE,{"derivedFrom":makeQuery(id+"F2.opExtrude","SWEPT_FACE",FACE,{"disambiguationData":[OSD([sQuery(id+"F0.wireOp",EDGE,"E13.1.2")])]})});
            var sketch = newSketch(context, id + "F6", { "sketchPlane" : qUnion([Q0])});
            skLineSegment(sketch, "E32", {"start": v(33.05, 0) * mm, "end": v(33.05, 2.8) * mm});
            skLineSegment(sketch, "E33", {"start": v(33.05, 2.8) * mm, "end": v(34.55, 2.8) * mm});
            skLineSegment(sketch, "E34", {"start": v(33.05, 2.8) * mm, "end": v(33.05, 8.8) * mm});
            skLineSegment(sketch, "E35", {"start": v(33.05, 8.8) * mm, "end": v(34.55, 6) * mm});
            skSolve(sketch);
        }
        {
            var Q0;
            {var subQ2=sQuery(id+"F6.wireOp",EDGE,"E35");Q0=makeQuery(id+"F6.imprint","IMPRINT",FACE,{"disambiguationData":[TD([[makeQuery(id+"F6.imprint","IMPRINT",EDGE,{"derivedFrom":subQ2}),-1.0]])]});}
            var Q1;
            {var subQ0=sQuery(id+"F6.wireOp",EDGE,"E33");Q1=makeQuery(id+"F6.imprint","IMPRINT",FACE,{"disambiguationData":[TD([[makeQuery(id+"F6.imprint","IMPRINT",EDGE,{"derivedFrom":subQ0}),1.0]])]});}
            var Q2;
            {var subQ0=sQuery(id+"F5.wireOp",EDGE,"E29");Q2=makeQuery(id+"F5.imprint","IMPRINT",FACE,{"disambiguationData":[TD([[makeQuery(id+"F5.imprint","IMPRINT",EDGE,{"derivedFrom":subQ0}),1.0]])]});}
            var Q3;
            {var subQ2=sQuery(id+"F5.wireOp",EDGE,"E31");Q3=makeQuery(id+"F5.imprint","IMPRINT",FACE,{"disambiguationData":[TD([[makeQuery(id+"F5.imprint","IMPRINT",EDGE,{"derivedFrom":subQ2}),-1.0]])]});}
            var Q4;
            {var subQ0=sQuery(id+"F4.wireOp",EDGE,"E24");Q4=makeQuery(id+"F4.imprint","IMPRINT",FACE,{"disambiguationData":[TD([[makeQuery(id+"F4.imprint","IMPRINT",EDGE,{"derivedFrom":subQ0}),1.0]])]});}
            var Q5;
            {var subQ2=sQuery(id+"F4.wireOp",EDGE,"E26");Q5=makeQuery(id+"F4.imprint","IMPRINT",FACE,{"disambiguationData":[TD([[makeQuery(id+"F4.imprint","IMPRINT",EDGE,{"derivedFrom":subQ2}),-1.0]])]});}
            var Q6;
            {var subQ0=sQuery(id+"F3.wireOp",EDGE,"E16");Q6=makeQuery(id+"F3.imprint","IMPRINT",FACE,{"disambiguationData":[TD([[makeQuery(id+"F3.imprint","IMPRINT",EDGE,{"derivedFrom":subQ0}),1.0]])]});}
            var Q7;
            Q7=makeQuery(id+"F3.imprint","IMPRINT",FACE,{"disambiguationData":[TD([[makeQuery(id+"F3.imprint","IMPRINT",EDGE,{"derivedFrom":sQuery(id+"F3.wireOp",EDGE,"E19")}),-1.0]])]});
            var Q8;
            Q8=sQuery(id+"F3.wireOp",EDGE,"E22");
            revolve(context, id + "F7", {"operationType" : NewBodyOperationType.REMOVE, "entities" : qUnion([Q0, Q1, Q2, Q3, Q4, Q5, Q6, Q7]), "axis" : qUnion([Q8]), "revolveType" : RevolveType.ONE_DIRECTION, "oppositeDirection" : true, "angle" : 15 * degree});
        }
        {
            var Q0;
            Q0=makeQuery(id+"F7.boolean.opBoolean","COPY",FACE,{"derivedFrom":makeQuery(id+"F7.opRevolve","CAP_FACE",FACE,{"disambiguationData":[OSD([sQuery(id+"F0.wireOp",EDGE,"E12.1.0"),sQuery(id+"F0.wireOp",EDGE,"E12.1.1"),sQuery(id+"F4.wireOp",EDGE,"E24"),sQuery(id+"F4.wireOp",EDGE,"E25"),sQuery(id+"F4.wireOp",EDGE,"E26")]),OD(0.0)],"isStart":false})});
            var Q1;
            Q1=makeQuery(id+"F7.boolean.opBoolean","COPY",FACE,{"derivedFrom":makeQuery(id+"F7.opRevolve","CAP_FACE",FACE,{"disambiguationData":[OSD([sQuery(id+"F0.wireOp",EDGE,"E8"),sQuery(id+"F0.wireOp",EDGE,"E10.0"),sQuery(id+"F5.wireOp",EDGE,"E29"),sQuery(id+"F5.wireOp",EDGE,"E30"),sQuery(id+"F5.wireOp",EDGE,"E31")]),OD(1.0)],"isStart":false})});
            var Q2;
            Q2=makeQuery(id+"F7.boolean.opBoolean","COPY",FACE,{"derivedFrom":makeQuery(id+"F7.opRevolve","CAP_FACE",FACE,{"disambiguationData":[OSD([sQuery(id+"F0.wireOp",EDGE,"E13.1.1"),sQuery(id+"F0.wireOp",EDGE,"E13.1.2"),sQuery(id+"F6.wireOp",EDGE,"E33"),sQuery(id+"F6.wireOp",EDGE,"E34"),sQuery(id+"F6.wireOp",EDGE,"E35")]),OD(1.0)],"isStart":false})});
            var Q3;
            Q3=makeQuery(id+"F7.boolean.opBoolean","COPY",FACE,{"derivedFrom":makeQuery(id+"F7.opRevolve","CAP_FACE",FACE,{"disambiguationData":[OSD([sQuery(id+"F0.wireOp",EDGE,"E0"),sQuery(id+"F0.wireOp",EDGE,"E14.1.1"),sQuery(id+"F0.wireOp",EDGE,"E14.1.2"),sQuery(id+"F3.wireOp",EDGE,"E16"),sQuery(id+"F3.wireOp",EDGE,"E19"),sQuery(id+"F3.wireOp",EDGE,"E20")])],"isStart":true})});
            var Q4;
            Q4=sQuery(id+"F3.wireOp",EDGE,"E22");
            revolve(context, id + "F8", {"operationType" : NewBodyOperationType.REMOVE, "entities" : qUnion([Q0, Q1, Q2, Q3]), "axis" : qUnion([Q4]), "revolveType" : RevolveType.ONE_DIRECTION, "angle" : 10.15 * degree});
        }
        {
            var Q0;
            Q0=makeQuery(id+"F1.opExtrude","CAP_EDGE",EDGE,{"disambiguationData":[OSD([sQuery(id+"F0.wireOp",EDGE,"E6.24.5")])],"isStart":true});
            chamfer(context, id + "F9", {"entities" : qUnion([Q0]), "width" : 0.2 * mm, "tangentPropagation" : true});
        }
        {
            var Q0;
            Q0=makeQuery(id+"F1.opExtrude","CAP_EDGE",EDGE,{"disambiguationData":[OSD([sQuery(id+"F0.wireOp",EDGE,"E6.13.5")])],"isStart":false});
            var Q1;
            Q1=makeQuery(id+"F1.opExtrude","CAP_EDGE",EDGE,{"disambiguationData":[OSD([sQuery(id+"F0.wireOp",EDGE,"E6.13.4")])],"isStart":false});
            var Q2;
            Q2=makeQuery(id+"F1.opExtrude","CAP_EDGE",EDGE,{"disambiguationData":[OSD([sQuery(id+"F0.wireOp",EDGE,"E6.13.0")])],"isStart":false});
            var Q3;
            Q3=makeQuery(id+"F1.opExtrude","CAP_EDGE",EDGE,{"disambiguationData":[OSD([sQuery(id+"F0.wireOp",EDGE,"E6.13.6"),sQuery(id+"F0.wireOp",EDGE,"E6.14.7")])],"isStart":false});
            var Q4;
            Q4=makeQuery(id+"F1.opExtrude","CAP_EDGE",EDGE,{"disambiguationData":[OSD([sQuery(id+"F0.wireOp",EDGE,"E6.14.5")])],"isStart":false});
            var Q5;
            Q5=makeQuery(id+"F1.opExtrude","CAP_EDGE",EDGE,{"disambiguationData":[OSD([sQuery(id+"F0.wireOp",EDGE,"E6.14.4")])],"isStart":false});
            var Q6;
            Q6=makeQuery(id+"F1.opExtrude","CAP_EDGE",EDGE,{"disambiguationData":[OSD([sQuery(id+"F0.wireOp",EDGE,"E6.14.0")])],"isStart":false});
            var Q7;
            Q7=makeQuery(id+"F1.opExtrude","CAP_EDGE",EDGE,{"disambiguationData":[OSD([sQuery(id+"F0.wireOp",EDGE,"E6.14.6"),sQuery(id+"F0.wireOp",EDGE,"E6.15.7")])],"isStart":false});
            var Q8;
            Q8=makeQuery(id+"F1.opExtrude","CAP_EDGE",EDGE,{"disambiguationData":[OSD([sQuery(id+"F0.wireOp",EDGE,"E6.15.5")])],"isStart":false});
            var Q9;
            Q9=makeQuery(id+"F1.opExtrude","CAP_EDGE",EDGE,{"disambiguationData":[OSD([sQuery(id+"F0.wireOp",EDGE,"E6.15.4")])],"isStart":false});
            var Q10;
            Q10=makeQuery(id+"F1.opExtrude","CAP_EDGE",EDGE,{"disambiguationData":[OSD([sQuery(id+"F0.wireOp",EDGE,"E6.15.0")])],"isStart":false});
            var Q11;
            Q11=makeQuery(id+"F1.opExtrude","CAP_EDGE",EDGE,{"disambiguationData":[OSD([sQuery(id+"F0.wireOp",EDGE,"E6.15.6"),sQuery(id+"F0.wireOp",EDGE,"E6.16.7")])],"isStart":false});
            var Q12;
            Q12=makeQuery(id+"F1.opExtrude","CAP_EDGE",EDGE,{"disambiguationData":[OSD([sQuery(id+"F0.wireOp",EDGE,"E6.16.5")])],"isStart":false});
            var Q13;
            Q13=makeQuery(id+"F1.opExtrude","CAP_EDGE",EDGE,{"disambiguationData":[OSD([sQuery(id+"F0.wireOp",EDGE,"E6.16.4")])],"isStart":false});
            var Q14;
            Q14=makeQuery(id+"F1.opExtrude","CAP_EDGE",EDGE,{"disambiguationData":[OSD([sQuery(id+"F0.wireOp",EDGE,"E6.16.0")])],"isStart":false});
            var Q15;
            Q15=makeQuery(id+"F1.opExtrude","CAP_EDGE",EDGE,{"disambiguationData":[OSD([sQuery(id+"F0.wireOp",EDGE,"E6.16.4")])],"isStart":false});
            var Q16;
            Q16=makeQuery(id+"F1.opExtrude","CAP_EDGE",EDGE,{"disambiguationData":[OSD([sQuery(id+"F0.wireOp",EDGE,"E6.16.6"),sQuery(id+"F0.wireOp",EDGE,"E6.17.7")])],"isStart":false});
            var Q17;
            Q17=makeQuery(id+"F1.opExtrude","CAP_EDGE",EDGE,{"disambiguationData":[OSD([sQuery(id+"F0.wireOp",EDGE,"E6.17.5")])],"isStart":false});
            var Q18;
            Q18=makeQuery(id+"F1.opExtrude","CAP_EDGE",EDGE,{"disambiguationData":[OSD([sQuery(id+"F0.wireOp",EDGE,"E6.17.4")])],"isStart":false});
            var Q19;
            Q19=makeQuery(id+"F1.opExtrude","CAP_EDGE",EDGE,{"disambiguationData":[OSD([sQuery(id+"F0.wireOp",EDGE,"E6.17.0")])],"isStart":false});
            var Q20;
            Q20=makeQuery(id+"F1.opExtrude","CAP_EDGE",EDGE,{"disambiguationData":[OSD([sQuery(id+"F0.wireOp",EDGE,"E6.17.6"),sQuery(id+"F0.wireOp",EDGE,"E6.18.7")])],"isStart":false});
            var Q21;
            Q21=makeQuery(id+"F1.opExtrude","CAP_EDGE",EDGE,{"disambiguationData":[OSD([sQuery(id+"F0.wireOp",EDGE,"E6.17.0")])],"isStart":false});
            var Q22;
            Q22=makeQuery(id+"F1.opExtrude","CAP_EDGE",EDGE,{"disambiguationData":[OSD([sQuery(id+"F0.wireOp",EDGE,"E6.18.5")])],"isStart":false});
            var Q23;
            Q23=makeQuery(id+"F1.opExtrude","CAP_EDGE",EDGE,{"disambiguationData":[OSD([sQuery(id+"F0.wireOp",EDGE,"E6.18.4")])],"isStart":false});
            var Q24;
            Q24=makeQuery(id+"F1.opExtrude","CAP_EDGE",EDGE,{"disambiguationData":[OSD([sQuery(id+"F0.wireOp",EDGE,"E6.18.0")])],"isStart":false});
            fillet(context, id + "F10", {"entities" : qUnion([Q0, Q1, Q2, Q3, Q4, Q5, Q6, Q7, Q8, Q9, Q10, Q11, Q12, Q13, Q14, Q15, Q16, Q17, Q18, Q19, Q20, Q21, Q22, Q23, Q24]), "radius" : 1 * mm, "tangentPropagation" : true, "allowEdgeOverflow" : false});
        }
        {
            var Q0;
            Q0=makeQuery(id+"F1.opExtrude","CAP_EDGE",EDGE,{"disambiguationData":[OSD([sQuery(id+"F0.wireOp",EDGE,"E0")])],"isStart":false});
            chamfer(context, id + "F11", {"entities" : qUnion([Q0]), "width" : 0.2 * mm, "tangentPropagation" : true});
        }
        {
            var Q0;
            Q0=makeQuery(id+"F8.boolean.opBoolean","COPY",EDGE,{"derivedFrom":makeQuery(id+"F8.opRevolve","CAP_EDGE",EDGE,{"disambiguationData":[OSD([sQuery(id+"F0.wireOp",EDGE,"E0"),sQuery(id+"F0.wireOp",EDGE,"E14.1.2"),sQuery(id+"F3.wireOp",EDGE,"E19")]),OD(0.0)],"isStart":false})});
            var Q1;
            Q1=makeQuery(id+"F2.boolean.opBoolean","COPY",EDGE,{"derivedFrom":makeQuery(id+"F2.opExtrude","SWEPT_EDGE",EDGE,{"disambiguationData":[OSD([sQuery(id+"F0.wireOp",EDGE,"E0"),sQuery(id+"F0.wireOp",EDGE,"E14.1.0")])]})});
            var Q2;
            Q2=makeQuery(id+"F7.boolean.opBoolean","COPY",EDGE,{"derivedFrom":makeQuery(id+"F7.opRevolve","CAP_EDGE",EDGE,{"disambiguationData":[OSD([sQuery(id+"F0.wireOp",EDGE,"E0"),sQuery(id+"F0.wireOp",EDGE,"E14.1.2"),sQuery(id+"F3.wireOp",EDGE,"E19")])],"isStart":false})});
            var Q3;
            Q3=makeQuery(id+"F2.boolean.opBoolean","COPY",EDGE,{"derivedFrom":makeQuery(id+"F2.opExtrude","SWEPT_EDGE",EDGE,{"disambiguationData":[OSD([sQuery(id+"F0.wireOp",EDGE,"E0"),sQuery(id+"F0.wireOp",EDGE,"E14.1.2")])]})});
            var Q4;
            Q4=makeQuery(id+"F2.boolean.opBoolean","COPY",EDGE,{"derivedFrom":makeQuery(id+"F2.opExtrude","SWEPT_EDGE",EDGE,{"disambiguationData":[OSD([sQuery(id+"F0.wireOp",EDGE,"E14.1.0"),sQuery(id+"F0.wireOp",EDGE,"E14.1.1")])]})});
            var Q5;
            Q5=makeQuery(id+"F2.boolean.opBoolean","COPY",EDGE,{"derivedFrom":makeQuery(id+"F2.opExtrude","SWEPT_EDGE",EDGE,{"disambiguationData":[OSD([sQuery(id+"F0.wireOp",EDGE,"E14.1.1"),sQuery(id+"F0.wireOp",EDGE,"E14.1.2")])]})});
            var Q6;
            Q6=makeQuery(id+"F7.boolean.opBoolean","COPY",EDGE,{"derivedFrom":makeQuery(id+"F7.opRevolve","CAP_EDGE",EDGE,{"disambiguationData":[OSD([sQuery(id+"F0.wireOp",EDGE,"E14.1.1"),sQuery(id+"F0.wireOp",EDGE,"E14.1.2")])],"isStart":false})});
            var Q7;
            Q7=makeQuery(id+"F7.boolean.opBoolean","COPY",EDGE,{"derivedFrom":makeQuery(id+"F7.opRevolve","CAP_EDGE",EDGE,{"disambiguationData":[OSD([sQuery(id+"F0.wireOp",EDGE,"E13.1.1"),sQuery(id+"F0.wireOp",EDGE,"E13.1.2")]),OD(0.0)],"isStart":false})});
            var Q8;
            Q8=makeQuery(id+"F7.boolean.opBoolean","COPY",EDGE,{"derivedFrom":makeQuery(id+"F7.opRevolve","CAP_EDGE",EDGE,{"disambiguationData":[OSD([sQuery(id+"F6.wireOp",EDGE,"E34")]),OD(0.0)],"isStart":false})});
            var Q9;
            Q9=makeQuery(id+"F2.boolean.opBoolean","COPY",EDGE,{"derivedFrom":makeQuery(id+"F2.opExtrude","SWEPT_EDGE",EDGE,{"disambiguationData":[OSD([sQuery(id+"F0.wireOp",EDGE,"E0"),sQuery(id+"F0.wireOp",EDGE,"E13.1.2")])]})});
            var Q10;
            Q10=makeQuery(id+"F2.boolean.opBoolean","COPY",EDGE,{"derivedFrom":makeQuery(id+"F2.opExtrude","SWEPT_EDGE",EDGE,{"disambiguationData":[OSD([sQuery(id+"F0.wireOp",EDGE,"E13.1.1"),sQuery(id+"F0.wireOp",EDGE,"E13.1.2")])]})});
            var Q11;
            Q11=makeQuery(id+"F8.boolean.opBoolean","COPY",EDGE,{"derivedFrom":makeQuery(id+"F8.opRevolve","CAP_EDGE",EDGE,{"disambiguationData":[OSD([sQuery(id+"F6.wireOp",EDGE,"E34")]),OD(1.0)],"isStart":false})});
            var Q12;
            Q12=makeQuery(id+"F2.boolean.opBoolean","COPY",EDGE,{"derivedFrom":makeQuery(id+"F2.opExtrude","SWEPT_EDGE",EDGE,{"disambiguationData":[OSD([sQuery(id+"F0.wireOp",EDGE,"E0"),sQuery(id+"F0.wireOp",EDGE,"E13.1.0")])]})});
            var Q13;
            Q13=makeQuery(id+"F2.boolean.opBoolean","COPY",EDGE,{"derivedFrom":makeQuery(id+"F2.opExtrude","SWEPT_EDGE",EDGE,{"disambiguationData":[OSD([sQuery(id+"F0.wireOp",EDGE,"E13.1.0"),sQuery(id+"F0.wireOp",EDGE,"E13.1.1")])]})});
            var Q14;
            Q14=makeQuery(id+"F7.boolean.opBoolean","COPY",EDGE,{"derivedFrom":makeQuery(id+"F7.opRevolve","CAP_EDGE",EDGE,{"disambiguationData":[OSD([sQuery(id+"F0.wireOp",EDGE,"E8"),sQuery(id+"F0.wireOp",EDGE,"E10.0")]),OD(0.0)],"isStart":false})});
            var Q15;
            Q15=makeQuery(id+"F7.boolean.opBoolean","COPY",EDGE,{"derivedFrom":makeQuery(id+"F7.opRevolve","CAP_EDGE",EDGE,{"disambiguationData":[OSD([sQuery(id+"F5.wireOp",EDGE,"E30")]),OD(0.0)],"isStart":false})});
            var Q16;
            Q16=makeQuery(id+"F2.boolean.opBoolean","COPY",EDGE,{"derivedFrom":makeQuery(id+"F2.opExtrude","SWEPT_EDGE",EDGE,{"disambiguationData":[OSD([sQuery(id+"F0.wireOp",EDGE,"E0"),sQuery(id+"F0.wireOp",EDGE,"E8")])]})});
            var Q17;
            Q17=makeQuery(id+"F2.boolean.opBoolean","COPY",EDGE,{"derivedFrom":makeQuery(id+"F2.opExtrude","SWEPT_EDGE",EDGE,{"disambiguationData":[OSD([sQuery(id+"F0.wireOp",EDGE,"E8"),sQuery(id+"F0.wireOp",EDGE,"E10.0")])]})});
            var Q18;
            Q18=makeQuery(id+"F8.boolean.opBoolean","COPY",EDGE,{"derivedFrom":makeQuery(id+"F8.opRevolve","CAP_EDGE",EDGE,{"disambiguationData":[OSD([sQuery(id+"F5.wireOp",EDGE,"E30")]),OD(1.0)],"isStart":false})});
            var Q19;
            Q19=makeQuery(id+"F2.boolean.opBoolean","COPY",EDGE,{"derivedFrom":makeQuery(id+"F2.opExtrude","SWEPT_EDGE",EDGE,{"disambiguationData":[OSD([sQuery(id+"F0.wireOp",EDGE,"E0"),sQuery(id+"F0.wireOp",EDGE,"E9")])]})});
            var Q20;
            Q20=makeQuery(id+"F2.boolean.opBoolean","COPY",EDGE,{"derivedFrom":makeQuery(id+"F2.opExtrude","SWEPT_EDGE",EDGE,{"disambiguationData":[OSD([sQuery(id+"F0.wireOp",EDGE,"E9"),sQuery(id+"F0.wireOp",EDGE,"E10.0")])]})});
            var Q21;
            Q21=makeQuery(id+"F7.boolean.opBoolean","COPY",EDGE,{"derivedFrom":makeQuery(id+"F7.opRevolve","CAP_EDGE",EDGE,{"disambiguationData":[OSD([sQuery(id+"F0.wireOp",EDGE,"E12.1.0"),sQuery(id+"F0.wireOp",EDGE,"E12.1.1")]),OD(1.0)],"isStart":false})});
            var Q22;
            Q22=makeQuery(id+"F7.boolean.opBoolean","COPY",EDGE,{"derivedFrom":makeQuery(id+"F7.opRevolve","CAP_EDGE",EDGE,{"disambiguationData":[OSD([sQuery(id+"F4.wireOp",EDGE,"E25")]),OD(1.0)],"isStart":false})});
            var Q23;
            Q23=makeQuery(id+"F2.boolean.opBoolean","COPY",EDGE,{"derivedFrom":makeQuery(id+"F2.opExtrude","SWEPT_EDGE",EDGE,{"disambiguationData":[OSD([sQuery(id+"F0.wireOp",EDGE,"E0"),sQuery(id+"F0.wireOp",EDGE,"E12.1.0")])]})});
            var Q24;
            Q24=makeQuery(id+"F2.boolean.opBoolean","COPY",EDGE,{"derivedFrom":makeQuery(id+"F2.opExtrude","SWEPT_EDGE",EDGE,{"disambiguationData":[OSD([sQuery(id+"F0.wireOp",EDGE,"E12.1.0"),sQuery(id+"F0.wireOp",EDGE,"E12.1.1")])]})});
            var Q25;
            Q25=makeQuery(id+"F2.boolean.opBoolean","COPY",EDGE,{"derivedFrom":makeQuery(id+"F2.opExtrude","SWEPT_EDGE",EDGE,{"disambiguationData":[OSD([sQuery(id+"F0.wireOp",EDGE,"E0"),sQuery(id+"F0.wireOp",EDGE,"E12.1.2")])]})});
            var Q26;
            Q26=makeQuery(id+"F8.boolean.opBoolean","COPY",EDGE,{"derivedFrom":makeQuery(id+"F8.opRevolve","CAP_EDGE",EDGE,{"disambiguationData":[OSD([sQuery(id+"F4.wireOp",EDGE,"E25")])],"isStart":false})});
            var Q27;
            Q27=makeQuery(id+"F2.boolean.opBoolean","COPY",EDGE,{"derivedFrom":makeQuery(id+"F2.opExtrude","SWEPT_EDGE",EDGE,{"disambiguationData":[OSD([sQuery(id+"F0.wireOp",EDGE,"E12.1.1"),sQuery(id+"F0.wireOp",EDGE,"E12.1.2")])]})});
            fillet(context, id + "F12", {"entities" : qUnion([Q0, Q1, Q2, Q3, Q4, Q5, Q6, Q7, Q8, Q9, Q10, Q11, Q12, Q13, Q14, Q15, Q16, Q17, Q18, Q19, Q20, Q21, Q22, Q23, Q24, Q25, Q26, Q27]), "radius" : 0.4 * mm, "tangentPropagation" : true, "allowEdgeOverflow" : false});
        }
        {
            var Q0;
            {var subQ0=sQuery(id+"F0.wireOp",EDGE,"E0");Q0=makeQuery(id+"F2.boolean.opBoolean","SPLIT",EDGE,{"disambiguationData":[TD([makeQuery(id+"F2.opExtrude","SWEPT_FACE",FACE,{"disambiguationData":[OSD([sQuery(id+"F0.wireOp",EDGE,"E12.1.2")])]})])],"derivedFrom":makeQuery(id+"F1.opExtrude","CAP_EDGE",EDGE,{"disambiguationData":[OSD([subQ0])],"isStart":true})});}
            var Q1;
            {var subQ0=sQuery(id+"F0.wireOp",EDGE,"E0");Q1=makeQuery(id+"F2.boolean.opBoolean","SPLIT",EDGE,{"disambiguationData":[TD([makeQuery(id+"F2.opExtrude","SWEPT_FACE",FACE,{"disambiguationData":[OSD([sQuery(id+"F0.wireOp",EDGE,"E13.1.2")])]})])],"derivedFrom":makeQuery(id+"F1.opExtrude","CAP_EDGE",EDGE,{"disambiguationData":[OSD([subQ0])],"isStart":true})});}
            var Q2;
            {var subQ0=sQuery(id+"F0.wireOp",EDGE,"E0");Q2=makeQuery(id+"F2.boolean.opBoolean","SPLIT",EDGE,{"disambiguationData":[TD([makeQuery(id+"F2.opExtrude","SWEPT_FACE",FACE,{"disambiguationData":[OSD([sQuery(id+"F0.wireOp",EDGE,"E8")])]})])],"derivedFrom":makeQuery(id+"F1.opExtrude","CAP_EDGE",EDGE,{"disambiguationData":[OSD([subQ0])],"isStart":true})});}
            var Q3;
            {var subQ0=sQuery(id+"F0.wireOp",EDGE,"E0");Q3=makeQuery(id+"F2.boolean.opBoolean","SPLIT",EDGE,{"disambiguationData":[TD([makeQuery(id+"F2.opExtrude","SWEPT_FACE",FACE,{"disambiguationData":[OSD([sQuery(id+"F0.wireOp",EDGE,"E9")])]})])],"derivedFrom":makeQuery(id+"F1.opExtrude","CAP_EDGE",EDGE,{"disambiguationData":[OSD([subQ0])],"isStart":true})});}
            chamfer(context, id + "F13", {"entities" : qUnion([Q0, Q1, Q2, Q3]), "width" : 0.2 * mm});
        }
    });
